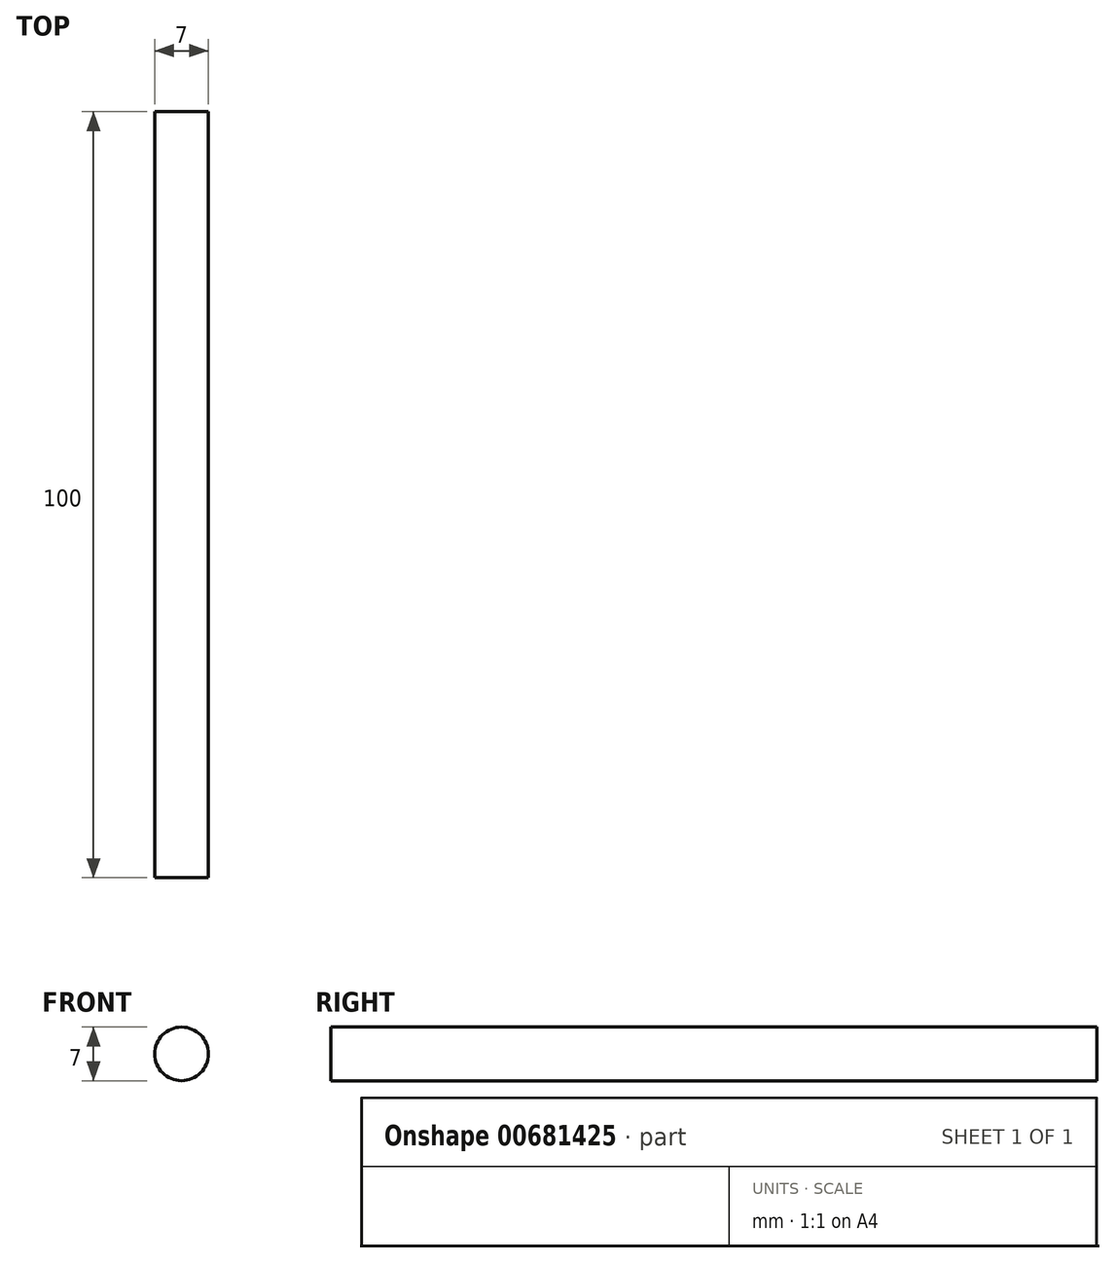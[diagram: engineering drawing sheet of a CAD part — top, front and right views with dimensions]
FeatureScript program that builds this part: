
annotation { "Feature Type Name" : "Feature", "Feature Type Description" : "" }
export const myFeature = defineFeature(function(context is Context, id is Id, definition is map)
    precondition{}
    {
        {
            var Q0;
            Q0=qCreatedBy(makeId("Front.planeOp"),FACE);
            var sketch = newSketch(context, id + "F0", { "sketchPlane" : qUnion([Q0])});
            skCircle(sketch, "E0", {"center": v(0, 0) * mm, "radius": 3.5 * mm});
            skSolve(sketch);
        }
        {
            var Q0;
            Q0 = qSketchRegion(id + "F0", true);
            extrude(context, id + "F1", {"entities" : qUnion([Q0]), "depth" : 100 * mm, "offsetDistance" : 25 * mm});
        }
    });
